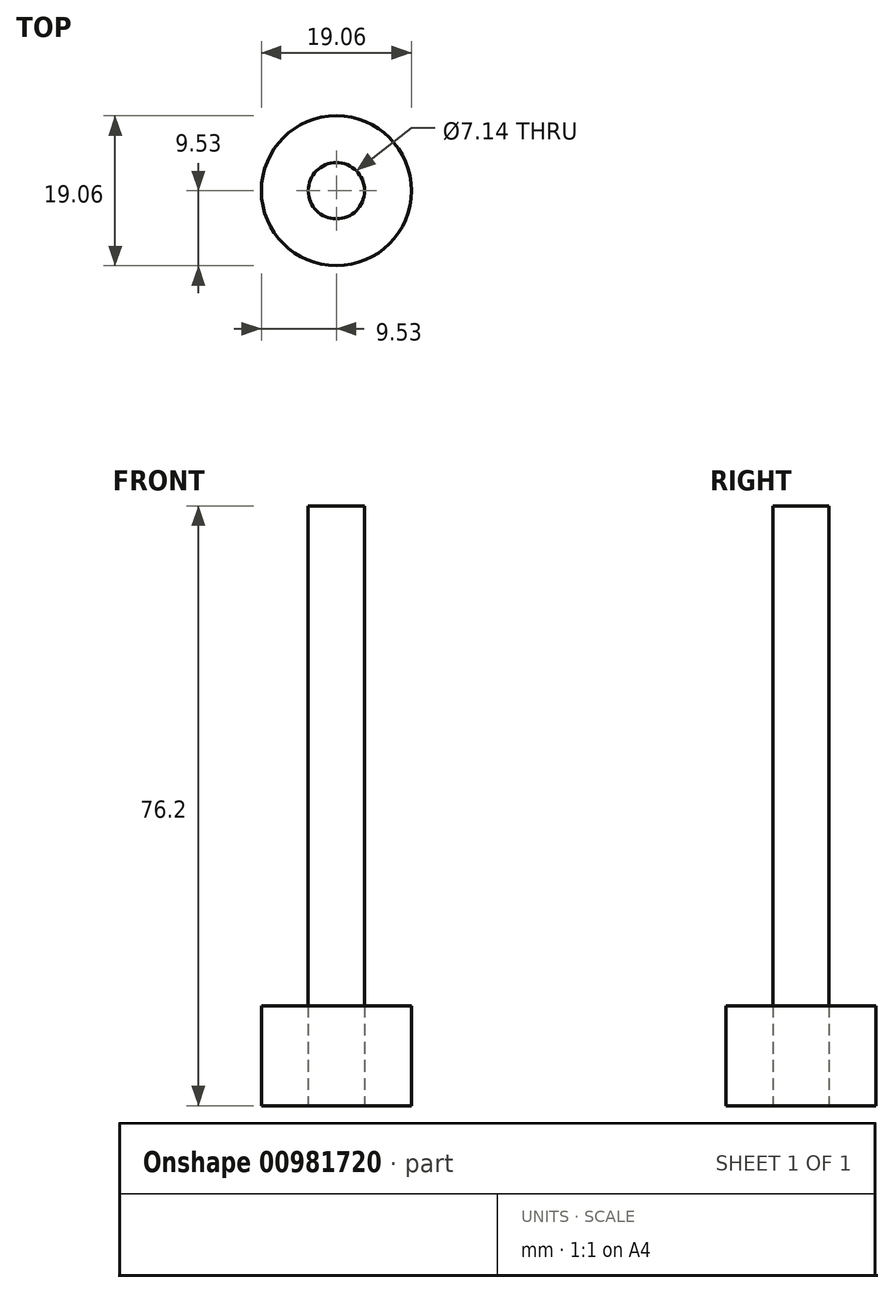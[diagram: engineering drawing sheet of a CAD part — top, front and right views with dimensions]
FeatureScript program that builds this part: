
annotation { "Feature Type Name" : "Feature", "Feature Type Description" : "" }
export const myFeature = defineFeature(function(context is Context, id is Id, definition is map)
    precondition{}
    {
        {
            var Q0;
            Q0=qCreatedBy(makeId("Top.planeOp"),FACE);
            var sketch = newSketch(context, id + "F0", { "sketchPlane" : qUnion([Q0])});
            skCircle(sketch, "E0", {"center": v(0, 0) * mm, "radius": 9.53 * mm});
            skCircle(sketch, "E1", {"center": v(0, 0) * mm, "radius": 3.57 * mm});
            skSolve(sketch);
        }
        {
            var Q0;
            Q0 = qSketchRegion(id + "F0", true);
            extrude(context, id + "F1", {"entities" : qUnion([Q0]), "depth" : 12.7 * mm, "offsetDistance" : 25.4 * mm});
        }
        {
            var Q0;
            Q0=makeQuery(id+"F0.imprint","IMPRINT",FACE,{"disambiguationData":[TD([[makeQuery(id+"F0.imprint","IMPRINT",EDGE,{"derivedFrom":sQuery(id+"F0.wireOp",EDGE,"E1")}),1.0]])]});
            extrude(context, id + "F2", {"entities" : qUnion([Q0]), "depth" : 76.2 * mm, "offsetDistance" : 25.4 * mm});
        }
    });
